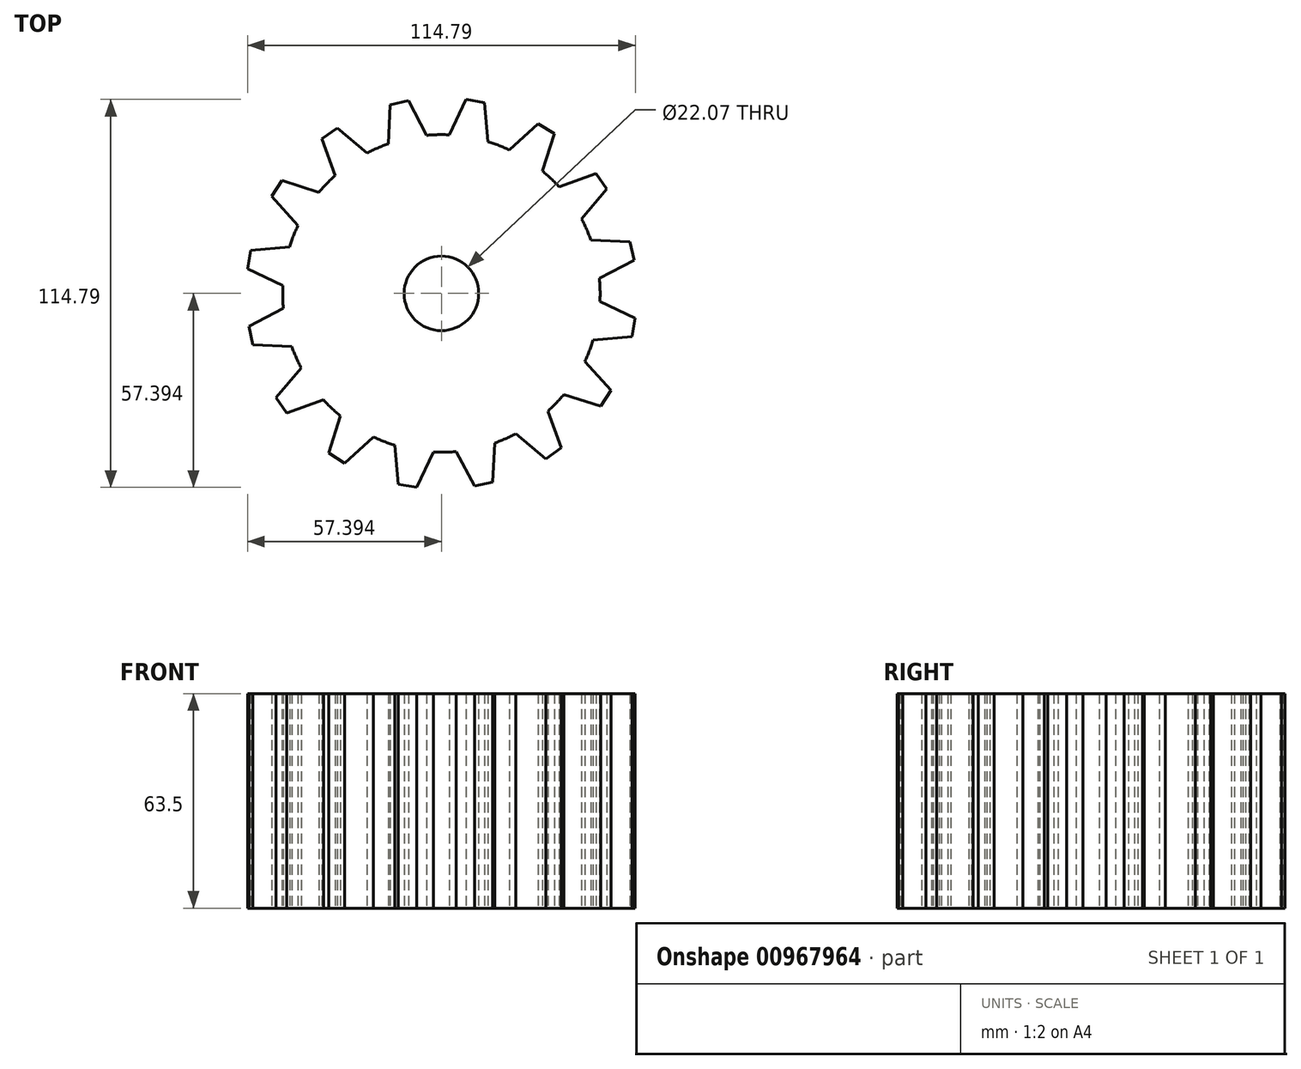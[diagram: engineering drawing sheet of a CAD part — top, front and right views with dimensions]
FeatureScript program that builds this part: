
annotation { "Feature Type Name" : "Feature", "Feature Type Description" : "" }
export const myFeature = defineFeature(function(context is Context, id is Id, definition is map)
    precondition{}
    {
        {
            var Q0;
            Q0=qCreatedBy(makeId("Top.planeOp"),FACE);
            var sketch = newSketch(context, id + "F0", { "sketchPlane" : qUnion([Q0])});
            skLineSegment(sketch, "E0", {"start": v(-28.13, 34.42) * mm, "end": v(-32.08, 45.28) * mm});
            skLineSegment(sketch, "E1", {"start": v(-32.08, 45.28) * mm, "end": v(-27.5, 48.48) * mm});
            skLineSegment(sketch, "E2", {"start": v(-27.5, 48.48) * mm, "end": v(-18.65, 41.06) * mm});
            skLineSegment(sketch, "E3.1.0", {"start": v(-39.09, 19.72) * mm, "end": v(-46.88, 28.24) * mm});
            skLineSegment(sketch, "E3.1.1", {"start": v(-43.88, 32.95) * mm, "end": v(-32.87, 29.48) * mm});
            skLineSegment(sketch, "E3.1.2", {"start": v(-46.88, 28.24) * mm, "end": v(-43.88, 32.95) * mm});
            skLineSegment(sketch, "E3.2.0", {"start": v(-43.58, 1.94) * mm, "end": v(-54.04, 6.83) * mm});
            skLineSegment(sketch, "E3.2.1", {"start": v(-53.07, 12.33) * mm, "end": v(-41.56, 13.34) * mm});
            skLineSegment(sketch, "E3.2.2", {"start": v(-54.04, 6.83) * mm, "end": v(-53.07, 12.33) * mm});
            skLineSegment(sketch, "E3.3.0", {"start": v(-40.92, -16.2) * mm, "end": v(-52.46, -15.7) * mm});
            skLineSegment(sketch, "E3.3.1", {"start": v(-53.67, -10.24) * mm, "end": v(-43.43, -4.9) * mm});
            skLineSegment(sketch, "E3.3.2", {"start": v(-52.46, -15.7) * mm, "end": v(-53.67, -10.24) * mm});
            skLineSegment(sketch, "E3.4.0", {"start": v(-31.53, -31.94) * mm, "end": v(-42.38, -35.89) * mm});
            skLineSegment(sketch, "E3.4.1", {"start": v(-45.58, -31.31) * mm, "end": v(-38.17, -22.46) * mm});
            skLineSegment(sketch, "E3.4.2", {"start": v(-42.38, -35.89) * mm, "end": v(-45.58, -31.31) * mm});
            skLineSegment(sketch, "E3.5.0", {"start": v(-16.82, -42.9) * mm, "end": v(-25.34, -50.7) * mm});
            skLineSegment(sketch, "E3.5.1", {"start": v(-30.05, -47.7) * mm, "end": v(-26.58, -36.68) * mm});
            skLineSegment(sketch, "E3.5.2", {"start": v(-25.34, -50.7) * mm, "end": v(-30.05, -47.7) * mm});
            skLineSegment(sketch, "E3.6.0", {"start": v(0.96, -47.39) * mm, "end": v(-3.93, -57.85) * mm});
            skLineSegment(sketch, "E3.6.1", {"start": v(-9.43, -56.88) * mm, "end": v(-10.44, -45.37) * mm});
            skLineSegment(sketch, "E3.6.2", {"start": v(-3.93, -57.85) * mm, "end": v(-9.43, -56.88) * mm});
            skLineSegment(sketch, "E3.7.0", {"start": v(19.1, -44.73) * mm, "end": v(18.59, -56.27) * mm});
            skLineSegment(sketch, "E3.7.1", {"start": v(13.13, -57.48) * mm, "end": v(7.8, -47.24) * mm});
            skLineSegment(sketch, "E3.7.2", {"start": v(18.59, -56.27) * mm, "end": v(13.13, -57.48) * mm});
            skLineSegment(sketch, "E3.8.0", {"start": v(34.84, -35.33) * mm, "end": v(38.79, -46.19) * mm});
            skLineSegment(sketch, "E3.8.1", {"start": v(34.2, -49.4) * mm, "end": v(25.36, -41.98) * mm});
            skLineSegment(sketch, "E3.8.2", {"start": v(38.79, -46.19) * mm, "end": v(34.2, -49.4) * mm});
            skPoint(sketch, "E3.center", {"position": v(3.35, -0.46) * mm});
            skLineSegment(sketch, "E4.1.9.0", {"start": v(45.8, -20.63) * mm, "end": v(53.59, -29.15) * mm});
            skLineSegment(sketch, "E4.3.9.0", {"start": v(50.59, -33.86) * mm, "end": v(39.57, -30.4) * mm});
            skLineSegment(sketch, "E4.6.9.0", {"start": v(53.59, -29.15) * mm, "end": v(50.59, -33.86) * mm});
            skLineSegment(sketch, "E4.1.10.0", {"start": v(50.28, -2.85) * mm, "end": v(60.75, -7.74) * mm});
            skLineSegment(sketch, "E4.3.10.0", {"start": v(59.78, -13.24) * mm, "end": v(48.27, -14.25) * mm});
            skLineSegment(sketch, "E4.6.10.0", {"start": v(60.75, -7.74) * mm, "end": v(59.78, -13.24) * mm});
            skLineSegment(sketch, "E5.1.11.0", {"start": v(47.63, 15.29) * mm, "end": v(59.16, 14.78) * mm});
            skLineSegment(sketch, "E5.3.11.0", {"start": v(60.37, 9.32) * mm, "end": v(50.13, 3.99) * mm});
            skLineSegment(sketch, "E5.6.11.0", {"start": v(59.16, 14.78) * mm, "end": v(60.37, 9.32) * mm});
            skLineSegment(sketch, "E5.1.12.0", {"start": v(38.23, 31.03) * mm, "end": v(49.09, 34.98) * mm});
            skLineSegment(sketch, "E5.3.12.0", {"start": v(52.3, 30.4) * mm, "end": v(44.87, 21.55) * mm});
            skLineSegment(sketch, "E5.6.12.0", {"start": v(49.09, 34.98) * mm, "end": v(52.3, 30.4) * mm});
            skLineSegment(sketch, "E5.1.13.0", {"start": v(23.53, 41.98) * mm, "end": v(32.05, 49.78) * mm});
            skLineSegment(sketch, "E5.3.13.0", {"start": v(36.76, 46.78) * mm, "end": v(33.3, 35.76) * mm});
            skLineSegment(sketch, "E5.6.13.0", {"start": v(32.05, 49.78) * mm, "end": v(36.76, 46.78) * mm});
            skLineSegment(sketch, "E5.1.14.0", {"start": v(5.75, 46.47) * mm, "end": v(10.64, 56.94) * mm});
            skLineSegment(sketch, "E5.3.14.0", {"start": v(16.14, 55.97) * mm, "end": v(17.15, 44.46) * mm});
            skLineSegment(sketch, "E5.6.14.0", {"start": v(10.64, 56.94) * mm, "end": v(16.14, 55.97) * mm});
            skLineSegment(sketch, "E5.1.15.0", {"start": v(-12.4, 43.82) * mm, "end": v(-11.88, 55.35) * mm});
            skLineSegment(sketch, "E5.3.15.0", {"start": v(-6.43, 56.56) * mm, "end": v(-1.09, 46.32) * mm});
            skLineSegment(sketch, "E5.6.15.0", {"start": v(-11.88, 55.35) * mm, "end": v(-6.43, 56.56) * mm});
            skArc(sketch, "E6", {"start": v(-43.58, 1.94) * mm, "mid": v(-43.63, -1.48) * mm, "end": v(-43.43, -4.9) * mm});
            skArc(sketch, "E7.trimOffspring", {"start": v(-40.92, -16.2) * mm, "mid": v(-39.66, -19.38) * mm, "end": v(-38.17, -22.46) * mm});
            skArc(sketch, "E8.trimOffspring", {"start": v(-31.53, -31.94) * mm, "mid": v(-29.14, -34.4) * mm, "end": v(-26.58, -36.68) * mm});
            skArc(sketch, "E9.trimOffspring", {"start": v(-16.82, -42.9) * mm, "mid": v(-13.68, -44.25) * mm, "end": v(-10.44, -45.37) * mm});
            skArc(sketch, "E10.trimOffspring", {"start": v(0.96, -47.39) * mm, "mid": v(4.38, -47.44) * mm, "end": v(7.8, -47.24) * mm});
            skArc(sketch, "E11.trimOffspring", {"start": v(19.1, -44.73) * mm, "mid": v(22.28, -43.47) * mm, "end": v(25.36, -41.98) * mm});
            skArc(sketch, "E12.trimOffspring", {"start": v(34.84, -35.33) * mm, "mid": v(37.3, -32.95) * mm, "end": v(39.57, -30.4) * mm});
            skArc(sketch, "E13.trimOffspring", {"start": v(45.8, -20.63) * mm, "mid": v(47.15, -17.49) * mm, "end": v(48.27, -14.25) * mm});
            skArc(sketch, "E14.trimOffspring", {"start": v(50.28, -2.85) * mm, "mid": v(50.33, 0.57) * mm, "end": v(50.13, 3.99) * mm});
            skArc(sketch, "E15.trimOffspring", {"start": v(47.63, 15.29) * mm, "mid": v(46.36, 18.47) * mm, "end": v(44.87, 21.55) * mm});
            skArc(sketch, "E16.trimOffspring", {"start": v(38.23, 31.03) * mm, "mid": v(35.85, 33.49) * mm, "end": v(33.3, 35.76) * mm});
            skArc(sketch, "E17.trimOffspring", {"start": v(23.53, 41.98) * mm, "mid": v(20.38, 43.34) * mm, "end": v(17.15, 44.46) * mm});
            skArc(sketch, "E18.trimOffspring", {"start": v(5.75, 46.47) * mm, "mid": v(2.33, 46.52) * mm, "end": v(-1.09, 46.32) * mm});
            skArc(sketch, "E19.trimOffspring", {"start": v(-12.4, 43.82) * mm, "mid": v(-15.57, 42.55) * mm, "end": v(-18.65, 41.06) * mm});
            skArc(sketch, "E20.trimOffspring", {"start": v(-28.13, 34.42) * mm, "mid": v(-30.6, 32.04) * mm, "end": v(-32.87, 29.48) * mm});
            skArc(sketch, "E21.trimOffspring", {"start": v(-39.09, 19.72) * mm, "mid": v(-40.44, 16.57) * mm, "end": v(-41.56, 13.34) * mm});
            skCircle(sketch, "E22", {"center": v(3.35, -0.46) * mm, "radius": 11.03 * mm});
            skSolve(sketch);
        }
        {
            var Q0;
            Q0=makeQuery(id+"F0.imprint","IMPRINT",FACE,{"disambiguationData":[TD([[makeQuery(id+"F0.imprint","IMPRINT",EDGE,{"derivedFrom":sQuery(id+"F0.wireOp",EDGE,"E0")}),-1.0]])]});
            extrude(context, id + "F1", {"entities" : qUnion([Q0]), "depth" : 63.5 * mm, "offsetDistance" : 25.4 * mm});
        }
    });
